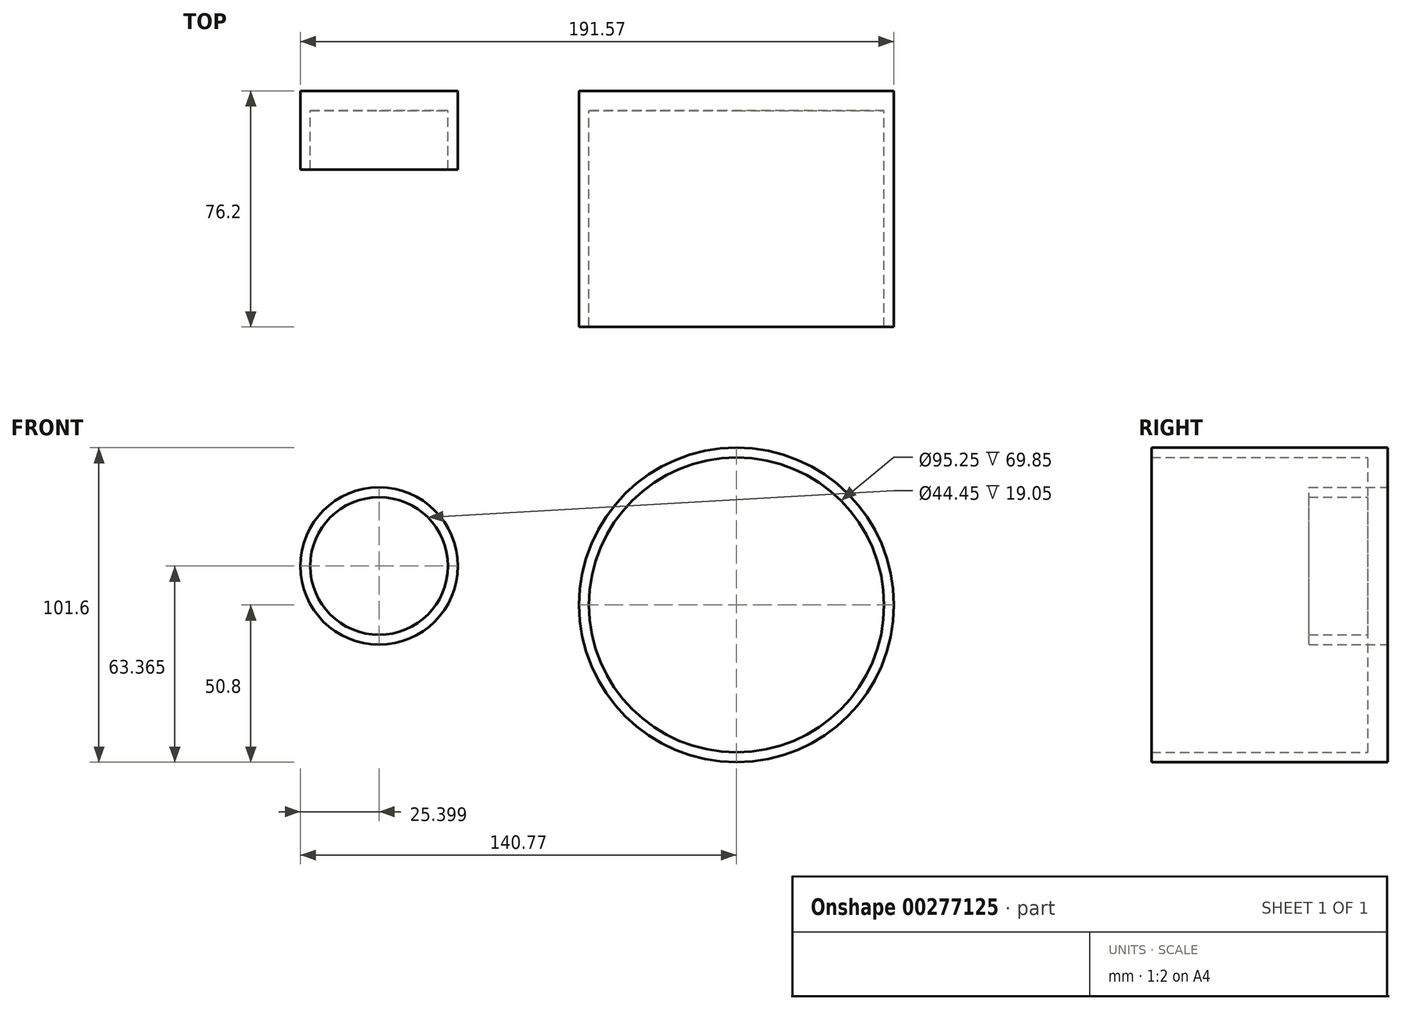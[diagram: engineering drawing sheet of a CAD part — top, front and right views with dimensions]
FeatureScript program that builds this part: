
annotation { "Feature Type Name" : "Feature", "Feature Type Description" : "" }
export const myFeature = defineFeature(function(context is Context, id is Id, definition is map)
    precondition{}
    {
        {
            var Q0;
            Q0=qCreatedBy(makeId("Front.planeOp"),FACE);
            var sketch = newSketch(context, id + "F0", { "sketchPlane" : qUnion([Q0])});
            skCircle(sketch, "E0", {"center": v(0, 0) * mm, "radius": 50.8 * mm});
            skCircle(sketch, "E1", {"center": v(0, 0) * mm, "radius": 47.63 * mm});
            skCircle(sketch, "E2", {"center": v(-115.37, 12.57) * mm, "radius": 25.4 * mm});
            skCircle(sketch, "E3", {"center": v(-115.37, 12.57) * mm, "radius": 22.23 * mm});
            skSolve(sketch);
        }
        {
            var Q0;
            Q0=makeQuery(id+"F0.imprint","IMPRINT",FACE,{"disambiguationData":[TD([[makeQuery(id+"F0.imprint","IMPRINT",EDGE,{"derivedFrom":sQuery(id+"F0.wireOp",EDGE,"E2")}),1.0]])]});
            extrude(context, id + "F1", {"entities" : qUnion([Q0]), "depth" : 25.4 * mm});
        }
        {
            var Q0;
            Q0=makeQuery(id+"F0.imprint","IMPRINT",FACE,{"disambiguationData":[TD([[makeQuery(id+"F0.imprint","IMPRINT",EDGE,{"derivedFrom":sQuery(id+"F0.wireOp",EDGE,"E0")}),1.0]])]});
            extrude(context, id + "F2", {"entities" : qUnion([Q0]), "depth" : 76.2 * mm});
        }
        {
            var Q0;
            Q0=makeQuery(id+"F0.imprint","IMPRINT",FACE,{"disambiguationData":[TD([[makeQuery(id+"F0.imprint","IMPRINT",EDGE,{"derivedFrom":sQuery(id+"F0.wireOp",EDGE,"E3")}),1.0]])]});
            extrude(context, id + "F3", {"entities" : qUnion([Q0]), "operationType" : NewBodyOperationType.ADD, "depth" : 6.35 * mm});
        }
        {
            var Q0;
            Q0=makeQuery(id+"F0.imprint","IMPRINT",FACE,{"disambiguationData":[TD([[makeQuery(id+"F0.imprint","IMPRINT",EDGE,{"derivedFrom":sQuery(id+"F0.wireOp",EDGE,"E1")}),1.0]])]});
            extrude(context, id + "F4", {"entities" : qUnion([Q0]), "operationType" : NewBodyOperationType.ADD, "depth" : 6.35 * mm});
        }
    });
